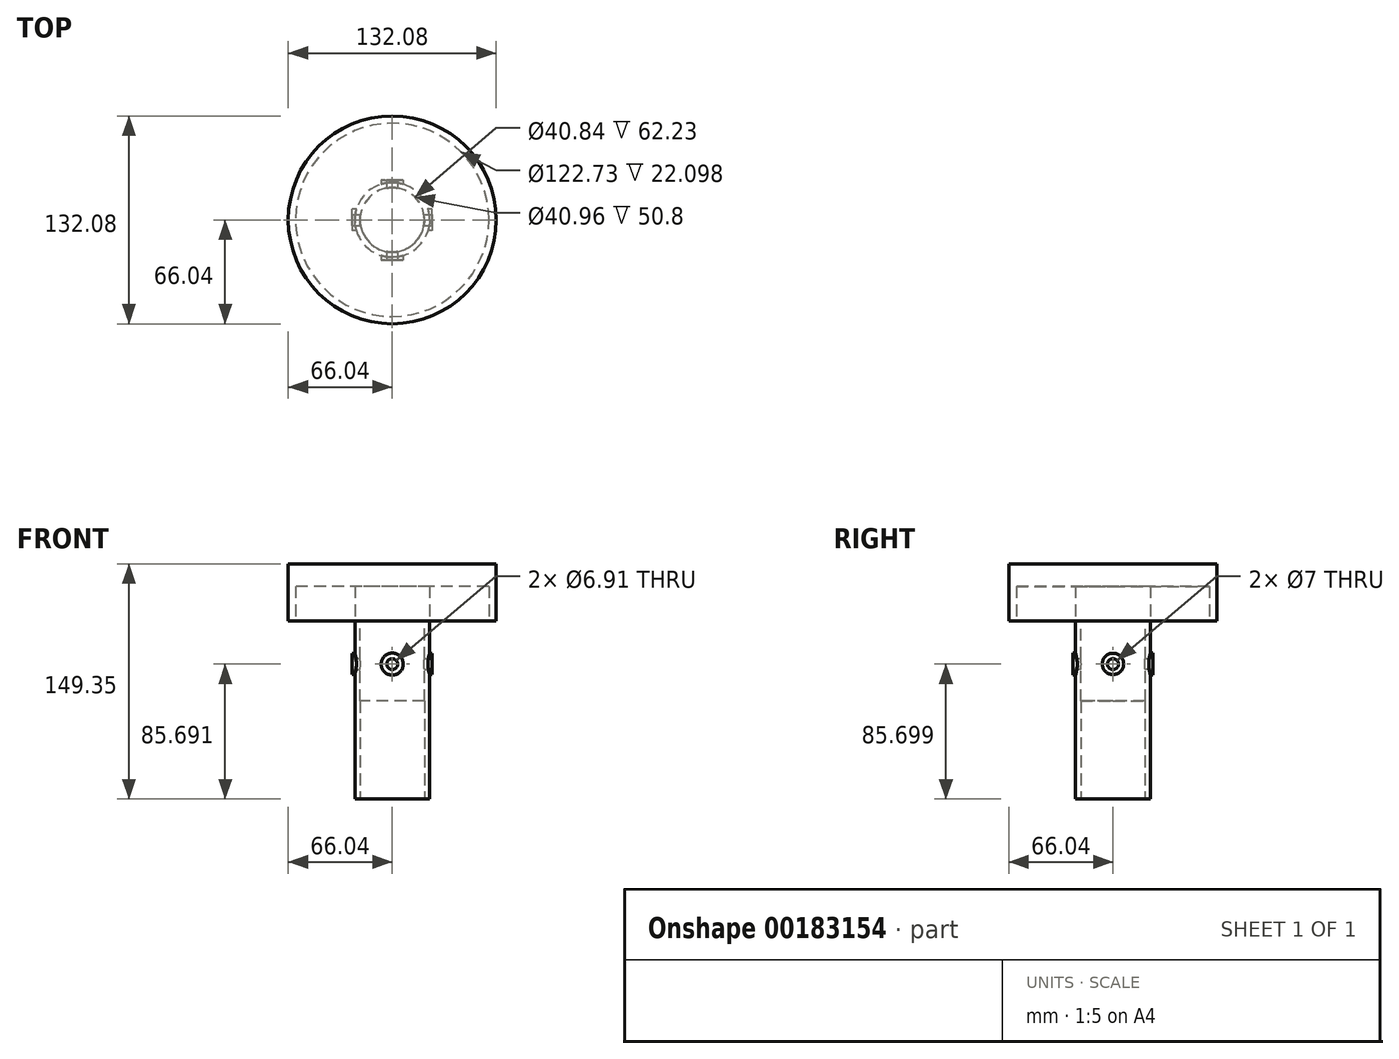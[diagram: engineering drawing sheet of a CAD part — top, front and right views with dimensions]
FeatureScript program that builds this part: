
annotation { "Feature Type Name" : "Feature", "Feature Type Description" : "" }
export const myFeature = defineFeature(function(context is Context, id is Id, definition is map)
    precondition{}
    {
        {
            var Q0;
            Q0=qCreatedBy(makeId("Top.planeOp"),FACE);
            var sketch = newSketch(context, id + "F0", { "sketchPlane" : qUnion([Q0])});
            skCircle(sketch, "E0", {"center": v(0, 0) * mm, "radius": 66.04 * mm});
            skSolve(sketch);
        }
        {
            var Q0;
            Q0 = qSketchRegion(id + "F0", true);
            extrude(context, id + "F1", {"entities" : qUnion([Q0]), "depth" : 36.32 * mm});
        }
        {
            var Q0;
            Q0=qCreatedBy(makeId("Top.planeOp"),FACE);
            var sketch = newSketch(context, id + "F2", { "sketchPlane" : qUnion([Q0])});
            skCircle(sketch, "E1", {"center": v(0, 0) * mm, "radius": 61.37 * mm});
            skSolve(sketch);
        }
        {
            var Q0;
            Q0=makeQuery(id+"F2.imprint","IMPRINT",FACE,{"disambiguationData":[TD([[makeQuery(id+"F2.imprint","IMPRINT",EDGE,{"derivedFrom":sQuery(id+"F2.wireOp",EDGE,"E1")}),1.0]])]});
            var Q1;
            Q1=sQuery(id+"F2.wireOp",EDGE,"E1");
            extrude(context, id + "F3", {"entities" : qUnion([Q0]), "operationType" : NewBodyOperationType.REMOVE, "surfaceEntities" : qUnion([Q1]), "depth" : 22.1 * mm});
        }
        {
            var Q0;
            Q0=qCreatedBy(makeId("Top.planeOp"),FACE);
            var sketch = newSketch(context, id + "F4", { "sketchPlane" : qUnion([Q0])});
            skCircle(sketch, "E2", {"center": v(0, 0) * mm, "radius": 23.75 * mm});
            skSolve(sketch);
        }
        {
            var Q0;
            Q0=makeQuery(id+"F4.imprint","IMPRINT",FACE,{"disambiguationData":[TD([[makeQuery(id+"F4.imprint","IMPRINT",EDGE,{"derivedFrom":sQuery(id+"F4.wireOp",EDGE,"E2")}),1.0]])]});
            var Q1;
            Q1=sQuery(id+"F4.wireOp",EDGE,"E2");
            extrude(context, id + "F5", {"entities" : qUnion([Q0]), "operationType" : NewBodyOperationType.ADD, "surfaceEntities" : qUnion([Q1]), "depth" : 23.62 * mm});
        }
        {
            var Q0;
            Q0=makeQuery(id+"F5.opExtrude","CAP_FACE",FACE,{"disambiguationData":[OSD([sQuery(id+"F4.wireOp",EDGE,"E2")])],"isStart":true});
            extrude(context, id + "F6", {"entities" : qUnion([Q0]), "operationType" : NewBodyOperationType.ADD, "depth" : 113.03 * mm});
        }
        {
            var Q0;
            Q0=makeQuery(id+"F6.opExtrude","CAP_FACE",FACE,{"disambiguationData":[OSD([sQuery(id+"F4.wireOp",EDGE,"E2")])],"isStart":false});
            var sketch = newSketch(context, id + "F7", { "sketchPlane" : qUnion([Q0])});
            skCircle(sketch, "E3", {"center": v(0, 0) * mm, "radius": 20.42 * mm});
            skSolve(sketch);
        }
        {
            var Q0;
            Q0 = qSketchRegion(id + "F7", true);
            extrude(context, id + "F8", {"entities" : qUnion([Q0]), "operationType" : NewBodyOperationType.REMOVE, "oppositeDirection" : true, "depth" : 101.6 * mm});
        }
        {
            var Q0;
            Q0=qCreatedBy(makeId("Front.planeOp"),FACE);
            var sketch = newSketch(context, id + "F9", { "sketchPlane" : qUnion([Q0])});
            skCircle(sketch, "E4", {"center": v(0, -18.81) * mm, "radius": 4.96 * mm});
            skSolve(sketch);
        }
        {
            var Q0;
            Q0 = qSketchRegion(id + "F9", true);
            extrude(context, id + "F10", {"entities" : qUnion([Q0]), "operationType" : NewBodyOperationType.ADD, "depth" : 12.7 * mm});
        }
        {
            var Q0;
            Q0=makeQuery(id+"F10.opExtrude","CAP_FACE",FACE,{"disambiguationData":[OSD([sQuery(id+"F9.wireOp",EDGE,"E4")])],"isStart":true});
            extrude(context, id + "F11", {"entities" : qUnion([Q0]), "operationType" : NewBodyOperationType.ADD, "depth" : 10.15 * mm});
        }
        {
            var Q0;
            Q0=makeQuery(id+"F10.opExtrude","SWEPT_BODY",BODY,{"disambiguationData":[OSD([sQuery(id+"F9.wireOp",EDGE,"E4")])]});
            deleteBodies(context, id + "F12", {"entities" : qUnion([Q0])});
        }
        {
            var Q0;
            Q0=qCreatedBy(makeId("Front.planeOp"),FACE);
            var sketch = newSketch(context, id + "F13", { "sketchPlane" : qUnion([Q0])});
            skCircle(sketch, "E5", {"center": v(0, -27.34) * mm, "radius": 6.99 * mm});
            skSolve(sketch);
        }
        {
            var Q0;
            Q0 = qSketchRegion(id + "F13", true);
            extrude(context, id + "F14", {"entities" : qUnion([Q0]), "operationType" : NewBodyOperationType.ADD, "endBound" : BoundingType.SYMMETRIC, "oppositeDirection" : true, "depth" : 50.8 * mm});
        }
        {
            var Q0;
            Q0=qCreatedBy(makeId("Right.planeOp"),FACE);
            var sketch = newSketch(context, id + "F15", { "sketchPlane" : qUnion([Q0])});
            skCircle(sketch, "E6", {"center": v(0, -27.2) * mm, "radius": 6.8 * mm});
            skSolve(sketch);
        }
        {
            var Q0;
            Q0 = qSketchRegion(id + "F15", true);
            extrude(context, id + "F16", {"entities" : qUnion([Q0]), "operationType" : NewBodyOperationType.ADD, "endBound" : BoundingType.SYMMETRIC, "depth" : 50.8 * mm});
        }
        {
            var Q0;
            Q0=qCreatedBy(makeId("Right.planeOp"),FACE);
            var sketch = newSketch(context, id + "F17", { "sketchPlane" : qUnion([Q0])});
            skCircle(sketch, "E7", {"center": v(0, -27.33) * mm, "radius": 3.5 * mm});
            skSolve(sketch);
        }
        {
            var Q0;
            Q0 = qSketchRegion(id + "F17", true);
            extrude(context, id + "F18", {"entities" : qUnion([Q0]), "operationType" : NewBodyOperationType.REMOVE, "endBound" : BoundingType.SYMMETRIC, "oppositeDirection" : true, "depth" : 80.16 * mm});
        }
        {
            var Q0;
            Q0=makeQuery(id+"F14.opExtrude","CAP_FACE",FACE,{"disambiguationData":[OSD([sQuery(id+"F13.wireOp",EDGE,"E5")])],"isStart":true});
            var sketch = newSketch(context, id + "F19", { "sketchPlane" : qUnion([Q0])});
            skCircle(sketch, "E8", {"center": v(0, -27.34) * mm, "radius": 3.45 * mm});
            skSolve(sketch);
        }
        {
            var Q0;
            Q0 = qSketchRegion(id + "F19", true);
            extrude(context, id + "F20", {"entities" : qUnion([Q0]), "operationType" : NewBodyOperationType.REMOVE, "endBound" : BoundingType.SYMMETRIC, "oppositeDirection" : true, "depth" : 144.27 * mm});
        }
        {
            var Q0;
            Q0=qCreatedBy(makeId("Top.planeOp"),FACE);
            var sketch = newSketch(context, id + "F21", { "sketchPlane" : qUnion([Q0])});
            skCircle(sketch, "E9", {"center": v(0, 0) * mm, "radius": 20.48 * mm});
            skSolve(sketch);
        }
        {
            var Q0;
            Q0 = qSketchRegion(id + "F21", true);
            extrude(context, id + "F22", {"entities" : qUnion([Q0]), "operationType" : NewBodyOperationType.REMOVE, "oppositeDirection" : true, "depth" : 50.8 * mm});
        }
    });
